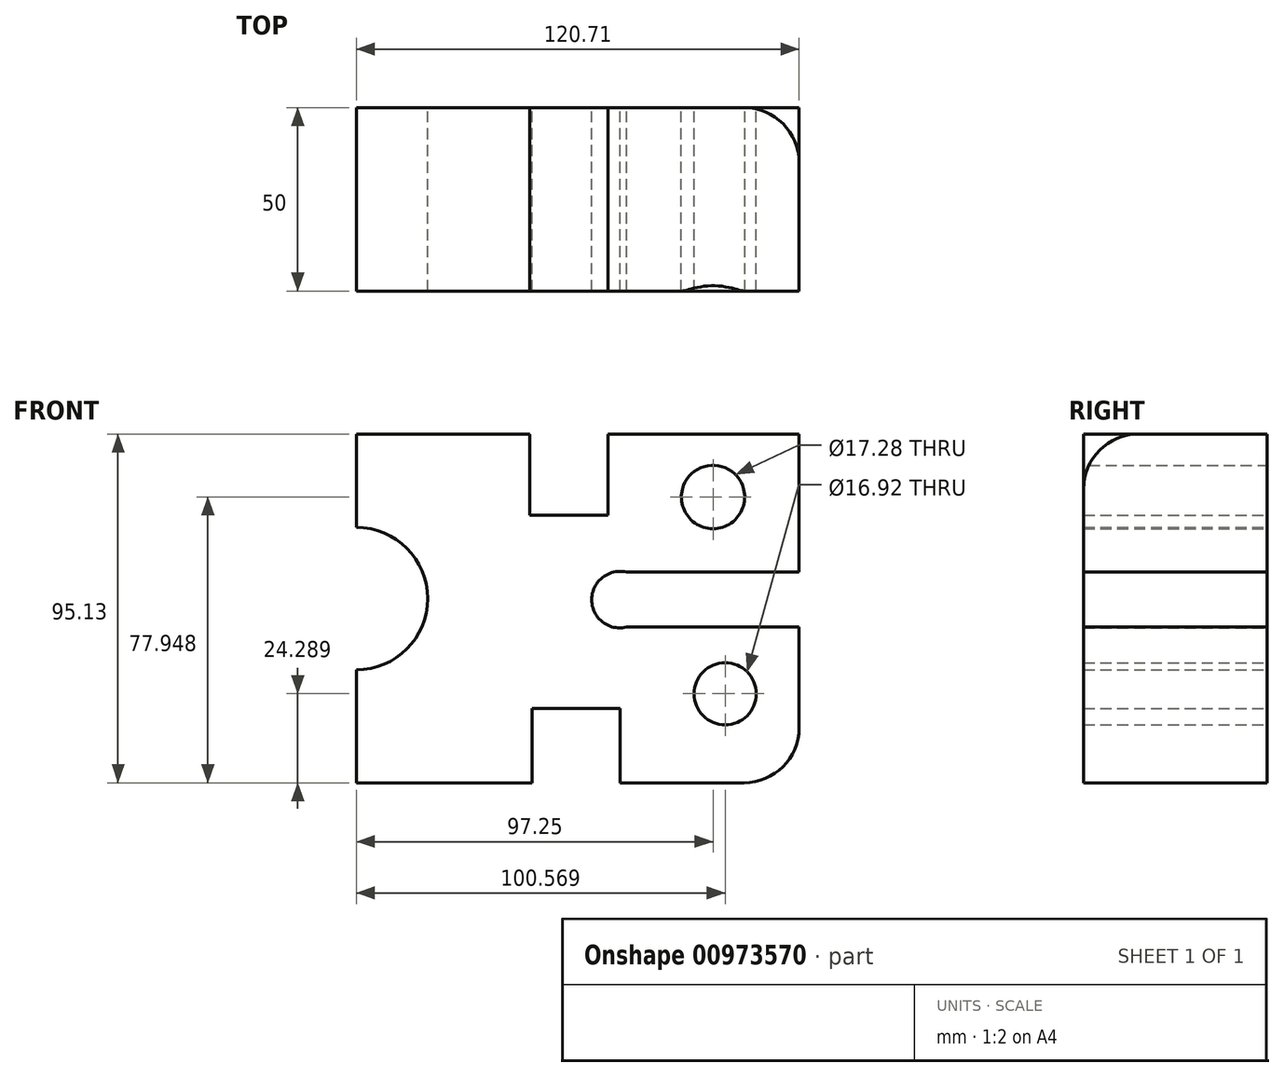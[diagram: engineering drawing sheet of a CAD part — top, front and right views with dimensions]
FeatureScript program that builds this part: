
annotation { "Feature Type Name" : "Feature", "Feature Type Description" : "" }
export const myFeature = defineFeature(function(context is Context, id is Id, definition is map)
    precondition{}
    {
        {
            var Q0;
            Q0=qCreatedBy(makeId("Front.planeOp"),FACE);
            var sketch = newSketch(context, id + "F0", { "sketchPlane" : qUnion([Q0])});
            skLineSegment(sketch, "E0.bottom", {"start": v(-60.12, 52.68) * mm, "end": v(-12.9, 52.68) * mm});
            skLineSegment(sketch, "E0.top", {"start": v(-60.12, -42.45) * mm, "end": v(-12.21, -42.45) * mm});
            skLineSegment(sketch, "E0.left", {"start": v(-60.12, 52.68) * mm, "end": v(-60.12, 27.2) * mm});
            skLineSegment(sketch, "E0.right", {"start": v(60.59, 52.68) * mm, "end": v(60.59, 15) * mm});
            skLineSegment(sketch, "E1.top", {"start": v(-12.9, 30.59) * mm, "end": v(8.49, 30.59) * mm});
            skLineSegment(sketch, "E1.left", {"start": v(-12.9, 52.68) * mm, "end": v(-12.9, 30.59) * mm});
            skLineSegment(sketch, "E1.right", {"start": v(8.49, 52.68) * mm, "end": v(8.49, 30.59) * mm});
            skLineSegment(sketch, "E2.bottom", {"start": v(60.59, 15) * mm, "end": v(11.75, 15) * mm});
            skLineSegment(sketch, "E2.top", {"start": v(60.59, 0) * mm, "end": v(11.75, 0) * mm});
            skPoint(sketch, "E3.oppositeSnap0", {"position": v(11.75, 7.5) * mm});
            skLineSegment(sketch, "E3.top", {"start": v(-12.21, -22.21) * mm, "end": v(11.75, -22.21) * mm});
            skLineSegment(sketch, "E3.left", {"start": v(-12.21, -42.45) * mm, "end": v(-12.21, -22.21) * mm});
            skLineSegment(sketch, "E3.right", {"start": v(11.75, -42.45) * mm, "end": v(11.75, -22.21) * mm});
            skArc(sketch, "E4", {"start": v(-60.12, -11.63) * mm, "mid": v(-40.7, 7.8) * mm, "end": v(-60.12, 27.2) * mm});
            skArc(sketch, "E5", {"start": v(13.53, 15) * mm, "mid": v(4.03, 7.5) * mm, "end": v(13.53, 0) * mm});
            skLineSegment(sketch, "E6.trimOffspring", {"start": v(-60.12, -11.63) * mm, "end": v(-60.12, -42.45) * mm});
            skLineSegment(sketch, "E7.trimOffspring", {"start": v(8.49, 52.68) * mm, "end": v(60.59, 52.68) * mm});
            skLineSegment(sketch, "E8.trimOffspring", {"start": v(11.75, -42.45) * mm, "end": v(60.59, -42.45) * mm});
            skLineSegment(sketch, "E9.trimOffspring", {"start": v(60.59, 0) * mm, "end": v(60.59, -42.45) * mm});
            skCircle(sketch, "E10", {"center": v(37.13, 35.5) * mm, "radius": 8.64 * mm});
            skCircle(sketch, "E11", {"center": v(40.45, -18.16) * mm, "radius": 8.46 * mm});
            skSolve(sketch);
        }
        {
            var Q0;
            Q0=makeQuery(id+"F0.imprint","IMPRINT",FACE,{"disambiguationData":[TD([[makeQuery(id+"F0.imprint","IMPRINT",EDGE,{"derivedFrom":sQuery(id+"F0.wireOp",EDGE,"E0.bottom")}),-1.0]])]});
            extrude(context, id + "F1", {"entities" : qUnion([Q0]), "depth" : 50 * mm, "offsetDistance" : 25 * mm});
        }
        {
            var Q0;
            Q0=makeQuery(id+"F1.opExtrude","CAP_EDGE",EDGE,{"disambiguationData":[OSD([sQuery(id+"F0.wireOp",EDGE,"E0.right")])],"isStart":true});
            fillet(context, id + "F2", {"entities" : qUnion([Q0]), "radius" : 15 * mm, "tangentPropagation" : true, "allowEdgeOverflow" : false});
        }
        {
            var Q0;
            Q0=makeQuery(id+"F1.opExtrude","SWEPT_EDGE",EDGE,{"disambiguationData":[OSD([sQuery(id+"F0.wireOp",EDGE,"E8.trimOffspring"),sQuery(id+"F0.wireOp",EDGE,"E9.trimOffspring")])]});
            fillet(context, id + "F3", {"entities" : qUnion([Q0]), "radius" : 15 * mm, "tangentPropagation" : true, "allowEdgeOverflow" : false});
        }
        {
            var Q0;
            Q0=makeQuery(id+"F1.opExtrude","CAP_EDGE",EDGE,{"disambiguationData":[OSD([sQuery(id+"F0.wireOp",EDGE,"E7.trimOffspring")])],"isStart":false});
            fillet(context, id + "F4", {"entities" : qUnion([Q0]), "radius" : 15 * mm, "tangentPropagation" : true, "allowEdgeOverflow" : false});
        }
    });
